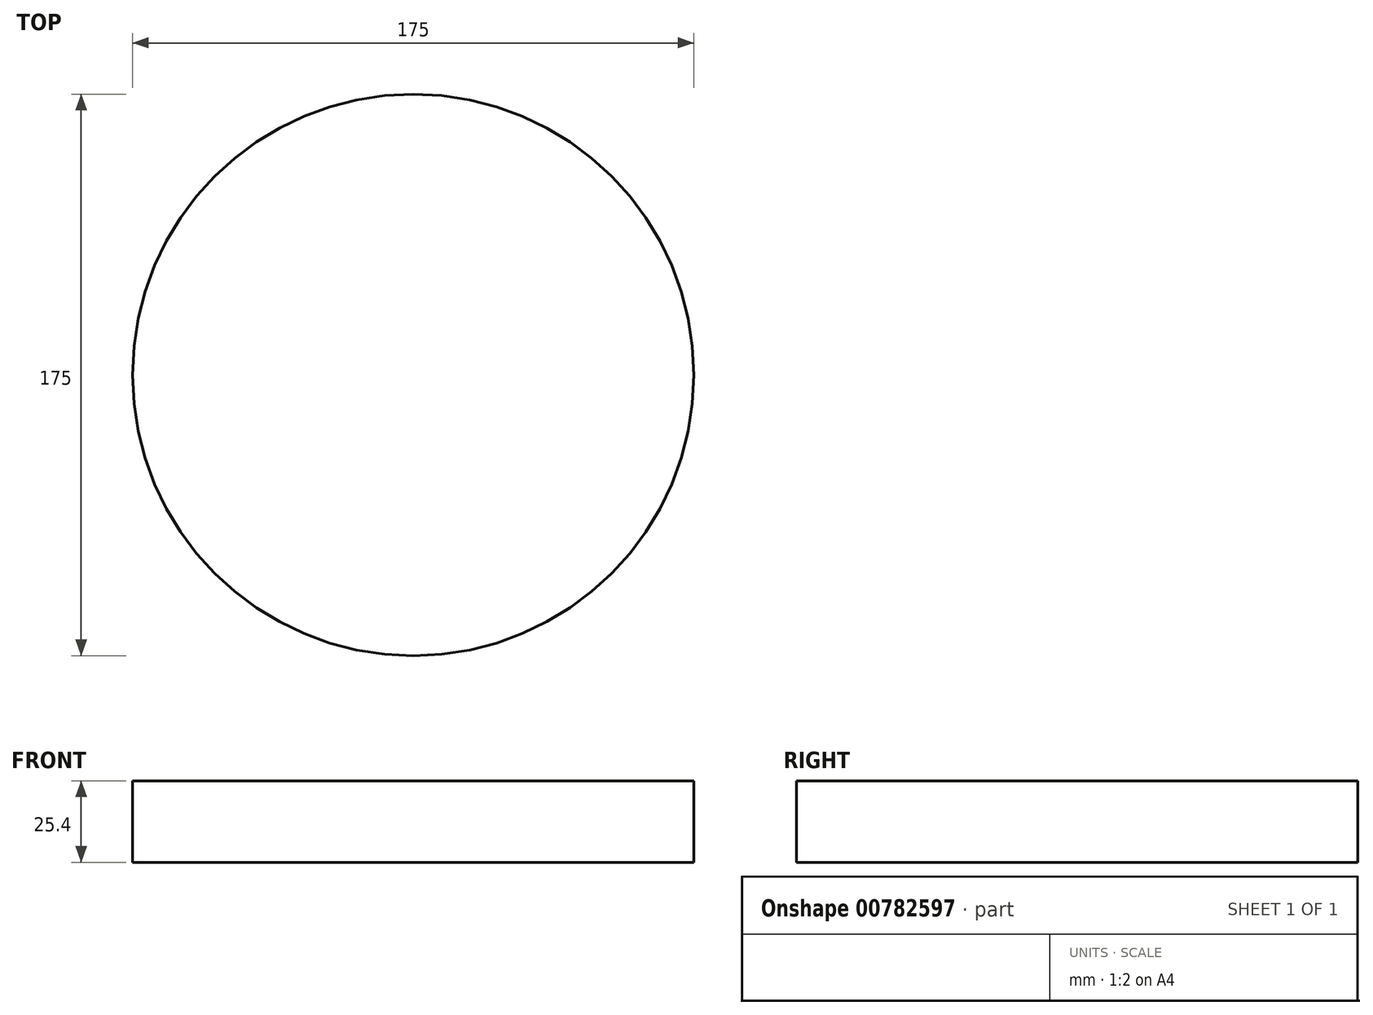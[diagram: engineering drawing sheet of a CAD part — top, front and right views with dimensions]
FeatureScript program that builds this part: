
annotation { "Feature Type Name" : "Feature", "Feature Type Description" : "" }
export const myFeature = defineFeature(function(context is Context, id is Id, definition is map)
    precondition{}
    {
        {
            var Q0;
            Q0=qCreatedBy(makeId("Top.planeOp"),FACE);
            var sketch = newSketch(context, id + "F0", { "sketchPlane" : qUnion([Q0])});
            skCircle(sketch, "E0", {"center": v(0, 0) * mm, "radius": 87.5 * mm});
            skLineSegment(sketch, "E1", {"start": v(0, 0) * mm, "end": v(83.22, 27.04) * mm});
            skSolve(sketch);
        }
        {
            var Q0;
            Q0 = qSketchRegion(id + "F0", true);
            extrude(context, id + "F1", {"entities" : qUnion([Q0]), "depth" : 25.4 * mm, "offsetDistance" : 25.4 * mm});
        }
    });
